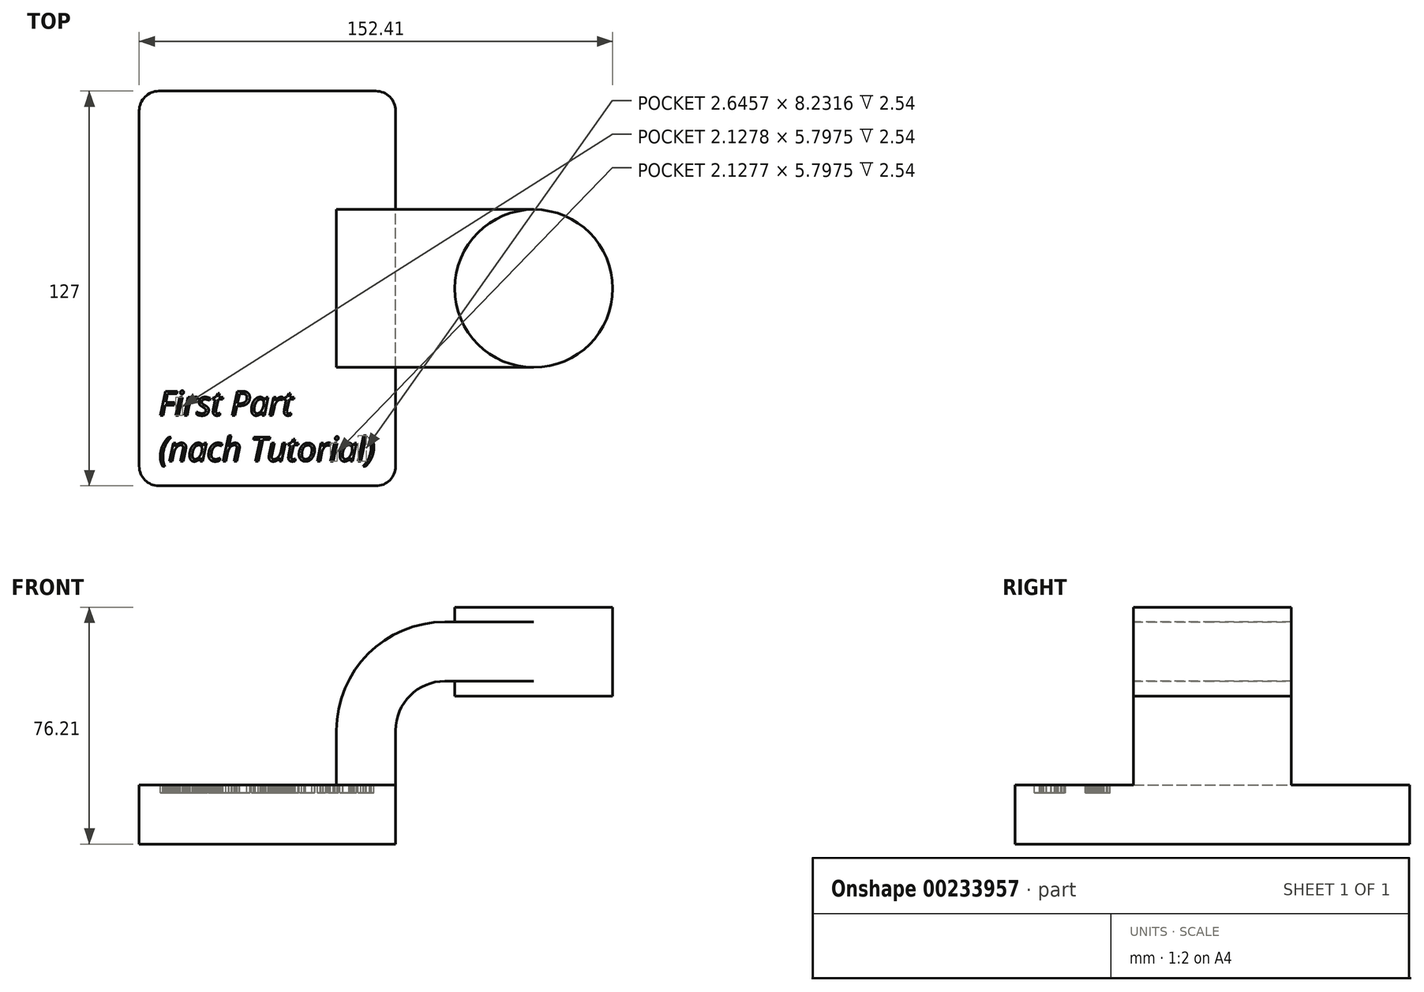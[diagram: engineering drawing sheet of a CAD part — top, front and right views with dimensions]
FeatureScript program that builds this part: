
annotation { "Feature Type Name" : "Feature", "Feature Type Description" : "" }
export const myFeature = defineFeature(function(context is Context, id is Id, definition is map)
    precondition{}
    {
        {
            var Q0;
            Q0=qCreatedBy(makeId("Front.planeOp"),FACE);
            var sketch = newSketch(context, id + "F0", { "sketchPlane" : qUnion([Q0])});
            skLineSegment(sketch, "E0.bottom", {"start": v(-41.28, -9.53) * mm, "end": v(41.28, -9.53) * mm});
            skLineSegment(sketch, "E0.top", {"start": v(-41.28, 9.53) * mm, "end": v(41.28, 9.53) * mm});
            skLineSegment(sketch, "E0.left", {"start": v(-41.28, -9.52) * mm, "end": v(-41.28, 9.52) * mm});
            skLineSegment(sketch, "E0.right", {"start": v(41.28, -9.52) * mm, "end": v(41.28, 9.52) * mm});
            skPoint(sketch, "E0.middle", {"position": v(0, 0) * mm});
            skLineSegment(sketch, "E1.bottom", {"start": v(111.12, 38.1) * mm, "end": v(60.32, 38.1) * mm});
            skLineSegment(sketch, "E1.top", {"start": v(111.12, 66.68) * mm, "end": v(60.32, 66.68) * mm});
            skLineSegment(sketch, "E1.left", {"start": v(111.12, 38.1) * mm, "end": v(111.12, 66.67) * mm});
            skLineSegment(sketch, "E1.right", {"start": v(60.32, 38.1) * mm, "end": v(60.32, 66.67) * mm});
            skPoint(sketch, "E1.middle", {"position": v(85.72, 52.39) * mm});
            skLineSegment(sketch, "E2", {"start": v(41.27, 9.52) * mm, "end": v(41.27, 27) * mm});
            skArc(sketch, "E3", {"start": v(41.27, 27) * mm, "mid": v(45.92, 38.23) * mm, "end": v(57.15, 42.88) * mm});
            skLineSegment(sketch, "E4", {"start": v(57.15, 42.88) * mm, "end": v(85.72, 42.88) * mm});
            skLineSegment(sketch, "E5.0", {"start": v(57.15, 61.93) * mm, "end": v(85.72, 61.93) * mm});
            skArc(sketch, "E5.1", {"start": v(22.23, 27) * mm, "mid": v(32.45, 51.7) * mm, "end": v(57.15, 61.93) * mm});
            skLineSegment(sketch, "E5.2", {"start": v(22.23, 9.52) * mm, "end": v(22.23, 27) * mm});
            skLineSegment(sketch, "E6", {"start": v(85.72, 38.1) * mm, "end": v(85.72, 66.68) * mm});
            skFitSpline(sketch, "E7", {"points": [v(-41.28, 9.53) * mm, v(57.15, 61.93) * mm], "startDerivative": vector(0.43, 56.7) * mm, "endDerivative": vector(114.64, -0.87) * mm});
            skSolve(sketch);
        }
        {
            var Q0;
            Q0=makeQuery(id+"F0.imprint","IMPRINT",FACE,{"disambiguationData":[TD([[makeQuery(id+"F0.imprint","IMPRINT",EDGE,{"derivedFrom":sQuery(id+"F0.wireOp",EDGE,"E0.bottom")}),1.0]])]});
            extrude(context, id + "F1", {"entities" : qUnion([Q0]), "endBound" : BoundingType.SYMMETRIC, "depth" : 127 * mm});
        }
        {
            var Q0;
            {var subQ1=sQuery(id+"F0.wireOp",EDGE,"E2");Q0=makeQuery(id+"F0.imprint","IMPRINT",FACE,{"disambiguationData":[TD([[makeQuery(id+"F0.imprint","IMPRINT",EDGE,{"derivedFrom":subQ1}),1.0]])]});}
            var Q1;
            {var subQ0=sQuery(id+"F0.wireOp",EDGE,"E4");var subQ1=sQuery(id+"F0.wireOp",EDGE,"E1.right");var subQ2=makeQuery(id+"F0.imprint","INTERSECT",VERTEX,{"derivedFrom":[subQ1,subQ0]});Q1=makeQuery(id+"F0.imprint","IMPRINT",FACE,{"disambiguationData":[TD([[makeQuery(id+"F0.imprint","IMPRINT",EDGE,{"disambiguationData":[TD([[subQ2,-1.0]])],"derivedFrom":subQ1}),-1.0]])]});}
            extrude(context, id + "F2", {"entities" : qUnion([Q0, Q1]), "operationType" : NewBodyOperationType.ADD, "endBound" : BoundingType.SYMMETRIC, "depth" : 50.8 * mm});
        }
        {
            var Q0;
            Q0=makeQuery(id+"F0.imprint","IMPRINT",FACE,{"disambiguationData":[TD([[makeQuery(id+"F0.imprint","IMPRINT",EDGE,{"derivedFrom":sQuery(id+"F0.wireOp",EDGE,"E5.1")}),1.0]])]});
            extrude(context, id + "F3", {"entities" : qUnion([Q0]), "operationType" : NewBodyOperationType.ADD, "endBound" : BoundingType.SYMMETRIC, "depth" : 15.88 * mm});
        }
        {
            var Q0;
            {var subQ0=sQuery(id+"F0.wireOp",EDGE,"E1.left");Q0=makeQuery(id+"F0.imprint","IMPRINT",FACE,{"disambiguationData":[TD([[makeQuery(id+"F0.imprint","IMPRINT",EDGE,{"derivedFrom":subQ0}),1.0]])]});}
            var Q1;
            Q1=sQuery(id+"F0.wireOp",EDGE,"E6");
            revolve(context, id + "F4", {"operationType" : NewBodyOperationType.ADD, "entities" : qUnion([Q0]), "axis" : qUnion([Q1]), "revolveType" : RevolveType.FULL});
        }
        {
            var Q0;
            Q0=makeQuery(id+"F1.opExtrude","CAP_EDGE",EDGE,{"disambiguationData":[OSD([sQuery(id+"F0.wireOp",EDGE,"E0.left")])],"isStart":false});
            var Q1;
            Q1=makeQuery(id+"F1.opExtrude","CAP_EDGE",EDGE,{"disambiguationData":[OSD([sQuery(id+"F0.wireOp",EDGE,"E0.right")])],"isStart":false});
            var Q2;
            Q2=makeQuery(id+"F1.opExtrude","CAP_EDGE",EDGE,{"disambiguationData":[OSD([sQuery(id+"F0.wireOp",EDGE,"E0.right")])],"isStart":true});
            var Q3;
            Q3=makeQuery(id+"F1.opExtrude","CAP_EDGE",EDGE,{"disambiguationData":[OSD([sQuery(id+"F0.wireOp",EDGE,"E0.left")])],"isStart":true});
            fillet(context, id + "F5", {"entities" : qUnion([Q0, Q1, Q2, Q3]), "radius" : 6.35 * mm, "tangentPropagation" : true, "allowEdgeOverflow" : false});
        }
        {
            var Q0;
            {var subQ3=sQuery(id+"F0.wireOp",EDGE,"E0.top");var subQ4=sQuery(id+"F0.wireOp",EDGE,"E0.right");var subQ5=sQuery(id+"F0.wireOp",EDGE,"E0.left");Q0=makeQuery(id+"F3.boolean.opBoolean","SPLIT",FACE,{"disambiguationData":[TD([makeQuery(id+"F1.opExtrude","CAP_FACE",FACE,{"disambiguationData":[OSD([sQuery(id+"F0.wireOp",EDGE,"E0.bottom"),subQ3,subQ5,subQ4])],"isStart":true})])],"derivedFrom":makeQuery(id+"F1.opExtrude","SWEPT_FACE",FACE,{"disambiguationData":[OSD([subQ3])]})});}
            var sketch = newSketch(context, id + "F6", { "sketchPlane" : qUnion([Q0])});
            skText(sketch, "E8", { "text": "First Part\n(nach Tutorial)", "fontName": "OpenSans-Italic.ttf"});
            const initialGuessF6  = {"E8": [-0.03493, -0.04081, 1, 0, 0.0078]};
            skSetInitialGuess(sketch, initialGuessF6);
            skSolve(sketch);
        }
        {
            var Q0;
            Q0 = qSketchRegion(id + "F6", true);
            extrude(context, id + "F7", {"entities" : qUnion([Q0]), "operationType" : NewBodyOperationType.REMOVE, "oppositeDirection" : true, "depth" : 2.54 * mm});
        }
    });
